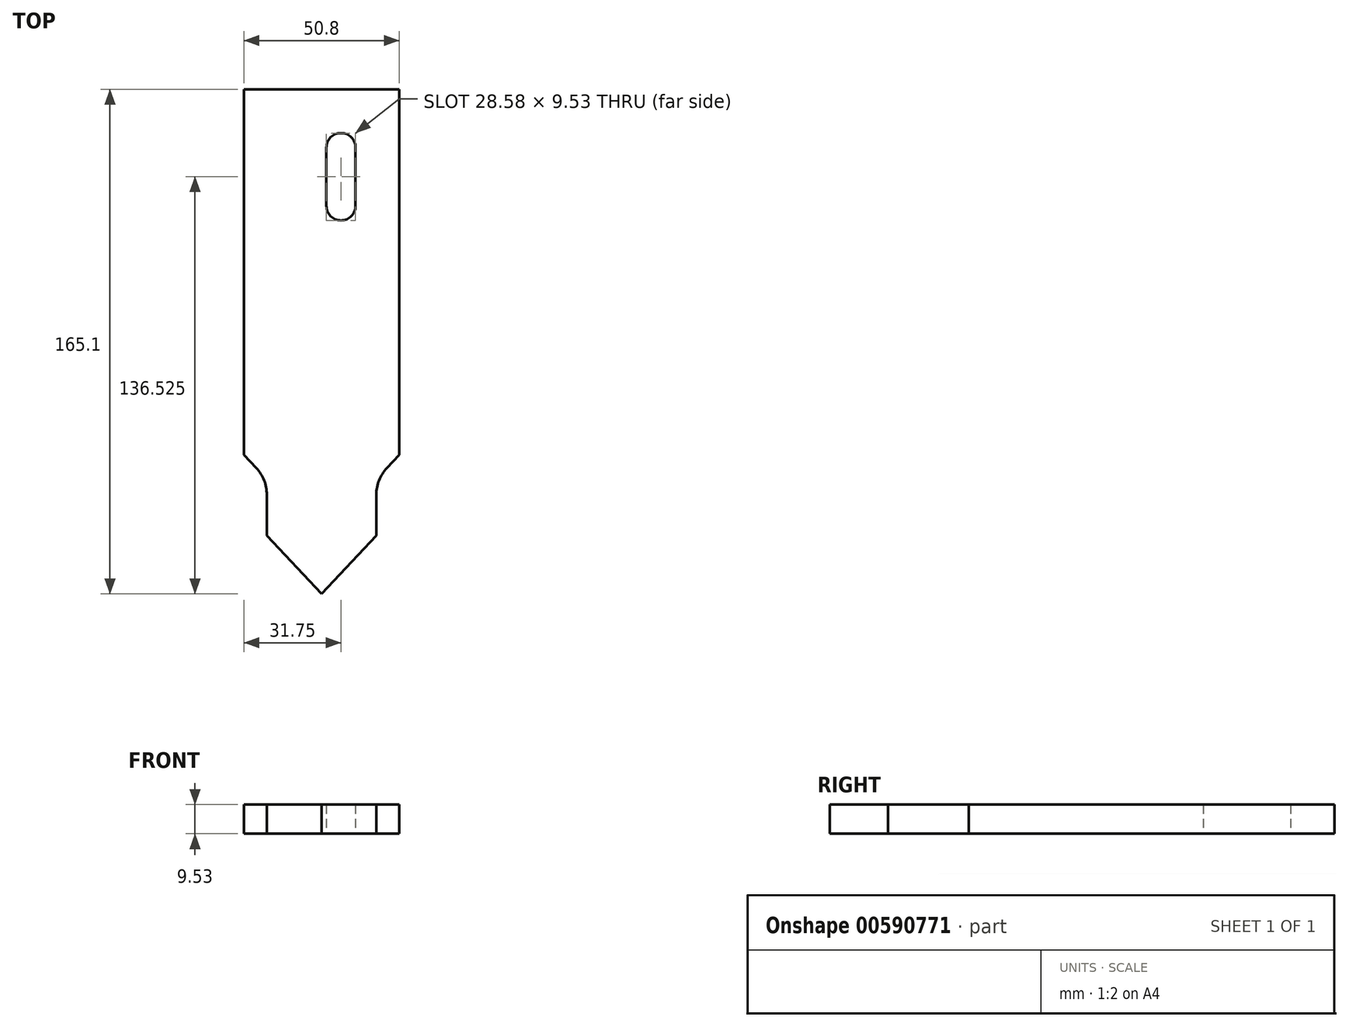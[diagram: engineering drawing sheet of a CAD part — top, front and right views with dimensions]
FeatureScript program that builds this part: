
annotation { "Feature Type Name" : "Feature", "Feature Type Description" : "" }
export const myFeature = defineFeature(function(context is Context, id is Id, definition is map)
    precondition{}
    {
        {
            var Q0;
            Q0=qCreatedBy(makeId("Top.planeOp"),FACE);
            var sketch = newSketch(context, id + "F0", { "sketchPlane" : qUnion([Q0])});
            skLineSegment(sketch, "E0.bottom", {"start": v(25.4, 82.55) * mm, "end": v(-25.4, 82.55) * mm});
            skLineSegment(sketch, "E0.left", {"start": v(25.4, 82.55) * mm, "end": v(25.4, -37.08) * mm});
            skLineSegment(sketch, "E0.right", {"start": v(-25.4, 82.55) * mm, "end": v(-25.4, -37.08) * mm});
            skPoint(sketch, "E0.middle", {"position": v(0, 0) * mm});
            skArc(sketch, "E1", {"start": v(11.11, 63.5) * mm, "mid": v(6.35, 68.26) * mm, "end": v(1.59, 63.5) * mm});
            skLineSegment(sketch, "E2", {"start": v(11.11, 63.5) * mm, "end": v(11.11, 44.45) * mm});
            skLineSegment(sketch, "E3", {"start": v(1.59, 63.5) * mm, "end": v(1.59, 44.45) * mm});
            skArc(sketch, "E4", {"start": v(1.59, 44.45) * mm, "mid": v(6.35, 39.69) * mm, "end": v(11.11, 44.45) * mm});
            skPoint(sketch, "E5.middle", {"position": v(0, -49.64) * mm});
            skLineSegment(sketch, "E6", {"start": v(-17.9, -63.5) * mm, "end": v(0, -82.55) * mm});
            skLineSegment(sketch, "E7", {"start": v(0, -82.55) * mm, "end": v(17.9, -63.5) * mm});
            skLineSegment(sketch, "E8.left", {"start": v(17.9, -63.5) * mm, "end": v(17.9, -50.09) * mm});
            skLineSegment(sketch, "E8.right", {"start": v(-17.9, -63.5) * mm, "end": v(-17.9, -50.09) * mm});
            skPoint(sketch, "E9.startSnap0", {"position": v(0, -37.08) * mm});
            skLineSegment(sketch, "E10", {"start": v(-25.4, -37.08) * mm, "end": v(-21.35, -41.39) * mm});
            skLineSegment(sketch, "E11.trimOffspring", {"start": v(21.35, -41.39) * mm, "end": v(25.4, -37.08) * mm});
            skPoint(sketch, "E12.visualSharp", {"position": v(-17.9, -45.06) * mm});
            skArc(sketch, "E12.filletArc", {"start": v(-17.9, -50.09) * mm, "mid": v(-18.8, -45.4) * mm, "end": v(-21.35, -41.39) * mm});
            skPoint(sketch, "E13.visualSharp", {"position": v(17.9, -45.06) * mm});
            skArc(sketch, "E13.filletArc", {"start": v(21.35, -41.39) * mm, "mid": v(18.8, -45.4) * mm, "end": v(17.9, -50.09) * mm});
            skSolve(sketch);
        }
        {
            var Q0;
            Q0 = qSketchRegion(id + "F0", true);
            extrude(context, id + "F1", {"entities" : qUnion([Q0]), "depth" : 9.52 * mm, "offsetDistance" : 25.4 * mm});
        }
    });
